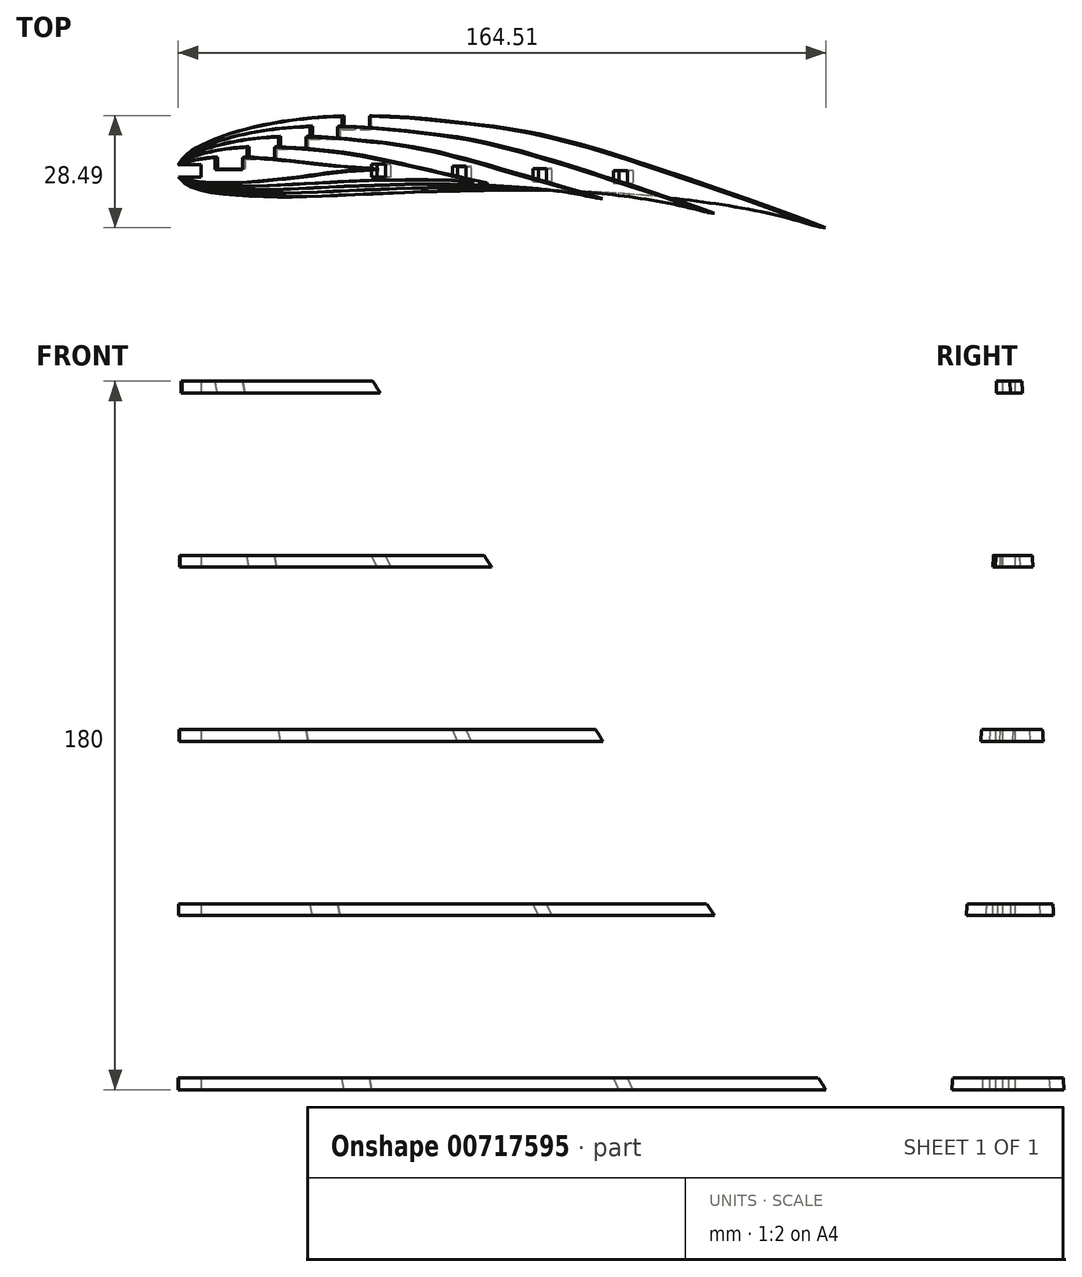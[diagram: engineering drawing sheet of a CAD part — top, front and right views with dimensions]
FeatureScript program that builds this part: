
annotation { "Feature Type Name" : "Feature", "Feature Type Description" : "" }
export const myFeature = defineFeature(function(context is Context, id is Id, definition is map)
    precondition{}
    {
        {
            var Q0;
            Q0=qCreatedBy(makeId("Top.planeOp"),FACE);
            var sketch = newSketch(context, id + "F0", { "sketchPlane" : qUnion([Q0])});
            skLineSegment(sketch, "E0", {"start": v(0.55, 2) * mm, "end": v(2.27, 4.06) * mm});
            skLineSegment(sketch, "E1", {"start": v(2.27, 4.06) * mm, "end": v(3.23, 4.97) * mm});
            skLineSegment(sketch, "E2", {"start": v(3.23, 4.97) * mm, "end": v(4.29, 5.76) * mm});
            skLineSegment(sketch, "E3", {"start": v(4.29, 5.76) * mm, "end": v(5.43, 6.47) * mm});
            skLineSegment(sketch, "E4", {"start": v(5.43, 6.47) * mm, "end": v(6.62, 7.1) * mm});
            skLineSegment(sketch, "E5", {"start": v(6.62, 7.1) * mm, "end": v(9.06, 8.22) * mm});
            skLineSegment(sketch, "E6", {"start": v(9.06, 8.22) * mm, "end": v(11.54, 9.18) * mm});
            skLineSegment(sketch, "E7", {"start": v(11.54, 9.18) * mm, "end": v(14.07, 10) * mm});
            skLineSegment(sketch, "E8", {"start": v(14.07, 10) * mm, "end": v(16.64, 10.72) * mm});
            skLineSegment(sketch, "E9", {"start": v(16.64, 10.72) * mm, "end": v(19.23, 11.35) * mm});
            skLineSegment(sketch, "E10", {"start": v(19.23, 11.35) * mm, "end": v(24.45, 12.45) * mm});
            skLineSegment(sketch, "E11", {"start": v(24.45, 12.45) * mm, "end": v(29.7, 13.34) * mm});
            skLineSegment(sketch, "E12", {"start": v(29.7, 13.34) * mm, "end": v(32.35, 13.68) * mm});
            skLineSegment(sketch, "E13", {"start": v(32.35, 13.68) * mm, "end": v(35, 13.95) * mm});
            skLineSegment(sketch, "E14", {"start": v(35, 13.95) * mm, "end": v(40.33, 14.29) * mm});
            skLineSegment(sketch, "E15", {"start": v(40.33, 14.29) * mm, "end": v(45.66, 14.43) * mm});
            skLineSegment(sketch, "E16", {"start": v(45.66, 14.43) * mm, "end": v(51, 14.4) * mm});
            skLineSegment(sketch, "E17", {"start": v(51, 14.4) * mm, "end": v(56.32, 14.18) * mm});
            skLineSegment(sketch, "E18", {"start": v(56.32, 14.18) * mm, "end": v(61.64, 13.83) * mm});
            skLineSegment(sketch, "E19", {"start": v(61.64, 13.83) * mm, "end": v(66.95, 13.36) * mm});
            skLineSegment(sketch, "E20", {"start": v(66.95, 13.36) * mm, "end": v(72.25, 12.79) * mm});
            skLineSegment(sketch, "E21", {"start": v(72.25, 12.79) * mm, "end": v(77.54, 12.1) * mm});
            skLineSegment(sketch, "E22", {"start": v(77.54, 12.1) * mm, "end": v(82.8, 11.26) * mm});
            skLineSegment(sketch, "E23", {"start": v(82.8, 11.26) * mm, "end": v(88.05, 10.28) * mm});
            skLineSegment(sketch, "E24", {"start": v(88.05, 10.28) * mm, "end": v(93.27, 9.2) * mm});
            skLineSegment(sketch, "E25", {"start": v(93.27, 9.2) * mm, "end": v(98.47, 8.03) * mm});
            skLineSegment(sketch, "E26", {"start": v(98.47, 8.03) * mm, "end": v(103.65, 6.76) * mm});
            skLineSegment(sketch, "E27", {"start": v(103.65, 6.76) * mm, "end": v(108.8, 5.4) * mm});
            skLineSegment(sketch, "E28", {"start": v(108.8, 5.4) * mm, "end": v(113.93, 3.92) * mm});
            skLineSegment(sketch, "E29", {"start": v(113.93, 3.92) * mm, "end": v(119.03, 2.37) * mm});
            skLineSegment(sketch, "E30", {"start": v(119.03, 2.37) * mm, "end": v(124.1, 0.73) * mm});
            skLineSegment(sketch, "E31", {"start": v(124.1, 0.73) * mm, "end": v(144.25, -6.3) * mm});
            skLineSegment(sketch, "E32", {"start": v(144.25, -6.3) * mm, "end": v(149.23, -8.12) * mm});
            skLineSegment(sketch, "E33", {"start": v(149.23, -8.12) * mm, "end": v(154.2, -10.04) * mm});
            skLineSegment(sketch, "E34", {"start": v(154.2, -10.04) * mm, "end": v(159.27, -11.88) * mm});
            skLineSegment(sketch, "E35", {"start": v(159.27, -11.88) * mm, "end": v(161.63, -12.76) * mm});
            skLineSegment(sketch, "E36", {"start": v(161.63, -12.76) * mm, "end": v(162.8, -13.22) * mm});
            skLineSegment(sketch, "E37", {"start": v(162.8, -13.22) * mm, "end": v(164.14, -13.73) * mm});
            skLineSegment(sketch, "E38", {"start": v(164.14, -13.73) * mm, "end": v(164.84, -13.98) * mm});
            skLineSegment(sketch, "E39", {"start": v(164.84, -13.98) * mm, "end": v(165, -14.04) * mm});
            skLineSegment(sketch, "E40", {"start": v(165, -14.04) * mm, "end": v(164.97, -14.04) * mm});
            skLineSegment(sketch, "E41", {"start": v(164.97, -14.04) * mm, "end": v(164.78, -14) * mm});
            skLineSegment(sketch, "E42", {"start": v(164.78, -14) * mm, "end": v(164.46, -13.9) * mm});
            skLineSegment(sketch, "E43", {"start": v(164.46, -13.9) * mm, "end": v(164.05, -13.77) * mm});
            skLineSegment(sketch, "E44", {"start": v(164.05, -13.77) * mm, "end": v(163.57, -13.62) * mm});
            skLineSegment(sketch, "E45", {"start": v(163.57, -13.62) * mm, "end": v(162.54, -13.3) * mm});
            skLineSegment(sketch, "E46", {"start": v(162.54, -13.3) * mm, "end": v(161.6, -13.02) * mm});
            skLineSegment(sketch, "E47", {"start": v(161.6, -13.02) * mm, "end": v(160.78, -12.78) * mm});
            skLineSegment(sketch, "E48", {"start": v(160.78, -12.78) * mm, "end": v(160.07, -12.58) * mm});
            skLineSegment(sketch, "E49", {"start": v(160.07, -12.58) * mm, "end": v(158.86, -12.25) * mm});
            skLineSegment(sketch, "E50", {"start": v(158.86, -12.25) * mm, "end": v(157.82, -11.99) * mm});
            skLineSegment(sketch, "E51", {"start": v(157.82, -11.99) * mm, "end": v(156.78, -11.74) * mm});
            skLineSegment(sketch, "E52", {"start": v(156.78, -11.74) * mm, "end": v(155.64, -11.47) * mm});
            skLineSegment(sketch, "E53", {"start": v(155.64, -11.47) * mm, "end": v(154.4, -11.18) * mm});
            skLineSegment(sketch, "E54", {"start": v(154.4, -11.18) * mm, "end": v(153.1, -10.88) * mm});
            skLineSegment(sketch, "E55", {"start": v(153.1, -10.88) * mm, "end": v(150.35, -10.26) * mm});
            skLineSegment(sketch, "E56", {"start": v(150.35, -10.26) * mm, "end": v(147.59, -9.68) * mm});
            skLineSegment(sketch, "E57", {"start": v(147.59, -9.68) * mm, "end": v(144.9, -9.16) * mm});
            skLineSegment(sketch, "E58", {"start": v(144.9, -9.16) * mm, "end": v(139.69, -8.28) * mm});
            skLineSegment(sketch, "E59", {"start": v(139.69, -8.28) * mm, "end": v(134.5, -7.54) * mm});
            skLineSegment(sketch, "E60", {"start": v(134.5, -7.54) * mm, "end": v(129.2, -6.88) * mm});
            skLineSegment(sketch, "E61", {"start": v(129.2, -6.88) * mm, "end": v(123.88, -6.3) * mm});
            skLineSegment(sketch, "E62", {"start": v(123.88, -6.3) * mm, "end": v(118.55, -5.81) * mm});
            skLineSegment(sketch, "E63", {"start": v(118.55, -5.81) * mm, "end": v(113.24, -5.41) * mm});
            skLineSegment(sketch, "E64", {"start": v(113.24, -5.41) * mm, "end": v(107.93, -5.1) * mm});
            skLineSegment(sketch, "E65", {"start": v(107.93, -5.1) * mm, "end": v(102.6, -4.84) * mm});
            skLineSegment(sketch, "E66", {"start": v(102.6, -4.84) * mm, "end": v(97.27, -4.67) * mm});
            skLineSegment(sketch, "E67", {"start": v(97.27, -4.67) * mm, "end": v(91.94, -4.58) * mm});
            skLineSegment(sketch, "E68", {"start": v(91.94, -4.58) * mm, "end": v(81.28, -4.6) * mm});
            skLineSegment(sketch, "E69", {"start": v(81.28, -4.6) * mm, "end": v(70.62, -4.85) * mm});
            skLineSegment(sketch, "E70", {"start": v(70.62, -4.85) * mm, "end": v(59.96, -5.2) * mm});
            skLineSegment(sketch, "E71", {"start": v(59.96, -5.2) * mm, "end": v(49.3, -5.55) * mm});
            skLineSegment(sketch, "E72", {"start": v(49.3, -5.55) * mm, "end": v(38.65, -5.97) * mm});
            skLineSegment(sketch, "E73", {"start": v(38.65, -5.97) * mm, "end": v(33.32, -6.17) * mm});
            skLineSegment(sketch, "E74", {"start": v(33.32, -6.17) * mm, "end": v(27.99, -6.29) * mm});
            skLineSegment(sketch, "E75", {"start": v(27.99, -6.29) * mm, "end": v(22.65, -6.26) * mm});
            skLineSegment(sketch, "E76", {"start": v(22.65, -6.26) * mm, "end": v(17.33, -6.03) * mm});
            skLineSegment(sketch, "E77", {"start": v(17.33, -6.03) * mm, "end": v(14.68, -5.81) * mm});
            skLineSegment(sketch, "E78", {"start": v(14.68, -5.81) * mm, "end": v(12.02, -5.5) * mm});
            skLineSegment(sketch, "E79", {"start": v(12.02, -5.5) * mm, "end": v(9.37, -5.1) * mm});
            skLineSegment(sketch, "E80", {"start": v(9.37, -5.1) * mm, "end": v(6.77, -4.56) * mm});
            skLineSegment(sketch, "E81", {"start": v(6.77, -4.56) * mm, "end": v(5.5, -4.23) * mm});
            skLineSegment(sketch, "E82", {"start": v(5.5, -4.23) * mm, "end": v(4.25, -3.83) * mm});
            skLineSegment(sketch, "E83", {"start": v(4.25, -3.83) * mm, "end": v(3.02, -3.3) * mm});
            skLineSegment(sketch, "E84", {"start": v(3.02, -3.3) * mm, "end": v(1.8, -2.61) * mm});
            skLineSegment(sketch, "E85", {"start": v(1.8, -2.61) * mm, "end": v(1.22, -2.19) * mm});
            skLineSegment(sketch, "E86", {"start": v(1.22, -2.19) * mm, "end": v(0.7, -1.71) * mm});
            skLineSegment(sketch, "E87", {"start": v(0.7, -1.71) * mm, "end": v(0.3, -1.19) * mm});
            skLineSegment(sketch, "E88", {"start": v(0.3, -1.19) * mm, "end": v(0.05, -0.62) * mm});
            skLineSegment(sketch, "E89", {"start": v(0.05, -0.62) * mm, "end": v(0, 0) * mm});
            skLineSegment(sketch, "E90", {"start": v(0, 0) * mm, "end": v(0.1, 0.65) * mm});
            skLineSegment(sketch, "E91", {"start": v(0.1, 0.65) * mm, "end": v(0.55, 2) * mm});
            skSolve(sketch);
        }
        {
            var Q0;
            Q0=qCreatedBy(makeId("Top.planeOp"),FACE);
            var sketch = newSketch(context, id + "F1", { "sketchPlane" : qUnion([Q0])});
            skPoint(sketch, "E92.0", {"position": v(0, 0) * mm});
            skPoint(sketch, "E92.1", {"position": v(3.23, 4.97) * mm});
            skPoint(sketch, "E92.2", {"position": v(0.55, 2) * mm});
            skPoint(sketch, "E92.3", {"position": v(16.64, 10.72) * mm});
            skPoint(sketch, "E92.4", {"position": v(45.66, 14.43) * mm});
            skPoint(sketch, "E92.5", {"position": v(77.54, 12.1) * mm});
            skPoint(sketch, "E92.6", {"position": v(108.8, 5.4) * mm});
            skPoint(sketch, "E92.7", {"position": v(165, -14.04) * mm});
            skPoint(sketch, "E92.8", {"position": v(156.78, -11.74) * mm});
            skPoint(sketch, "E92.9", {"position": v(129.2, -6.88) * mm});
            skPoint(sketch, "E92.10", {"position": v(91.94, -4.58) * mm});
            skPoint(sketch, "E92.11", {"position": v(49.3, -5.55) * mm});
            skPoint(sketch, "E92.12", {"position": v(27.99, -6.29) * mm});
            skPoint(sketch, "E92.13", {"position": v(12.02, -5.5) * mm});
            skPoint(sketch, "E92.14", {"position": v(3.02, -3.3) * mm});
            skFitSpline(sketch, "E93", {"points": [v(0.04, -0.4) * mm, v(0.59, 1.6) * mm, v(3.27, 4.57) * mm, v(16.67, 10.32) * mm, v(45.7, 14.03) * mm, v(77.58, 11.7) * mm, v(108.84, 4.99) * mm, v(165.04, -14.44) * mm, v(156.82, -12.14) * mm, v(129.25, -7.28) * mm, v(91.98, -4.98) * mm, v(49.34, -5.95) * mm, v(28.03, -6.69) * mm, v(12.06, -5.9) * mm, v(3.05, -3.7) * mm, v(0.04, -0.4) * mm]});
            skSolve(sketch);
        }
        {
            var Q0;
            Q0=qCreatedBy(makeId("Top.planeOp"),FACE);
            cPlane(context, id + "F2", {"entities" : qUnion([Q0]), "cplaneType" : CPlaneType.OFFSET, "offset" : 180 * mm, "width" : 150 * mm, "height" : 150 * mm});
        }
        {
            var Q0;
            Q0=qCreatedBy(id+"F2.planeOp",FACE);
            var sketch = newSketch(context, id + "F3", { "sketchPlane" : qUnion([Q0])});
            skLineSegment(sketch, "E94", {"start": v(0, 0) * mm, "end": v(0.15, 0.38) * mm});
            skLineSegment(sketch, "E95", {"start": v(0.15, 0.38) * mm, "end": v(0.35, 0.74) * mm});
            skLineSegment(sketch, "E96", {"start": v(0.35, 0.74) * mm, "end": v(0.46, 0.88) * mm});
            skLineSegment(sketch, "E97", {"start": v(0.46, 0.88) * mm, "end": v(0.6, 1.02) * mm});
            skLineSegment(sketch, "E98", {"start": v(0.6, 1.02) * mm, "end": v(0.92, 1.26) * mm});
            skLineSegment(sketch, "E99", {"start": v(0.92, 1.26) * mm, "end": v(1.29, 1.49) * mm});
            skLineSegment(sketch, "E100", {"start": v(1.29, 1.49) * mm, "end": v(1.63, 1.67) * mm});
            skLineSegment(sketch, "E101", {"start": v(1.63, 1.67) * mm, "end": v(2.36, 2) * mm});
            skLineSegment(sketch, "E102", {"start": v(2.36, 2) * mm, "end": v(2.87, 2.18) * mm});
            skLineSegment(sketch, "E103", {"start": v(2.87, 2.18) * mm, "end": v(3.88, 2.45) * mm});
            skLineSegment(sketch, "E104", {"start": v(3.88, 2.45) * mm, "end": v(5.05, 2.68) * mm});
            skLineSegment(sketch, "E105", {"start": v(5.05, 2.68) * mm, "end": v(7.03, 2.98) * mm});
            skLineSegment(sketch, "E106", {"start": v(7.03, 2.98) * mm, "end": v(7.78, 3.07) * mm});
            skLineSegment(sketch, "E107", {"start": v(7.78, 3.07) * mm, "end": v(8.62, 3.15) * mm});
            skLineSegment(sketch, "E108", {"start": v(8.62, 3.15) * mm, "end": v(10.95, 3.27) * mm});
            skLineSegment(sketch, "E109", {"start": v(10.95, 3.27) * mm, "end": v(11.82, 3.3) * mm});
            skLineSegment(sketch, "E110", {"start": v(11.82, 3.3) * mm, "end": v(13.41, 3.32) * mm});
            skLineSegment(sketch, "E111", {"start": v(13.41, 3.32) * mm, "end": v(14.62, 3.32) * mm});
            skLineSegment(sketch, "E112", {"start": v(14.62, 3.32) * mm, "end": v(16.6, 3.26) * mm});
            skLineSegment(sketch, "E113", {"start": v(16.6, 3.26) * mm, "end": v(18.58, 3.17) * mm});
            skLineSegment(sketch, "E114", {"start": v(18.58, 3.17) * mm, "end": v(21.4, 3.02) * mm});
            skLineSegment(sketch, "E115", {"start": v(21.4, 3.02) * mm, "end": v(22.8, 2.92) * mm});
            skLineSegment(sketch, "E116", {"start": v(22.8, 2.92) * mm, "end": v(24.58, 2.78) * mm});
            skLineSegment(sketch, "E117", {"start": v(24.58, 2.78) * mm, "end": v(27.06, 2.53) * mm});
            skLineSegment(sketch, "E118", {"start": v(27.06, 2.53) * mm, "end": v(31.42, 2.03) * mm});
            skLineSegment(sketch, "E119", {"start": v(31.42, 2.03) * mm, "end": v(35.63, 1.59) * mm});
            skLineSegment(sketch, "E120", {"start": v(35.63, 1.59) * mm, "end": v(37.3, 1.42) * mm});
            skLineSegment(sketch, "E121", {"start": v(37.3, 1.42) * mm, "end": v(39.54, 1.19) * mm});
            skLineSegment(sketch, "E122", {"start": v(39.54, 1.19) * mm, "end": v(42.05, 0.94) * mm});
            skLineSegment(sketch, "E123", {"start": v(42.05, 0.94) * mm, "end": v(43.06, 0.84) * mm});
            skLineSegment(sketch, "E124", {"start": v(43.06, 0.84) * mm, "end": v(44.5, 0.72) * mm});
            skLineSegment(sketch, "E125", {"start": v(44.5, 0.72) * mm, "end": v(45.29, 0.66) * mm});
            skLineSegment(sketch, "E126", {"start": v(45.29, 0.66) * mm, "end": v(45.98, 0.6) * mm});
            skLineSegment(sketch, "E127", {"start": v(45.98, 0.6) * mm, "end": v(46.75, 0.52) * mm});
            skLineSegment(sketch, "E128", {"start": v(46.75, 0.52) * mm, "end": v(47.13, 0.5) * mm});
            skLineSegment(sketch, "E129", {"start": v(47.13, 0.5) * mm, "end": v(47.54, 0.47) * mm});
            skLineSegment(sketch, "E130", {"start": v(47.54, 0.47) * mm, "end": v(48.16, 0.45) * mm});
            skLineSegment(sketch, "E131", {"start": v(48.16, 0.45) * mm, "end": v(48.52, 0.44) * mm});
            skLineSegment(sketch, "E132", {"start": v(48.52, 0.44) * mm, "end": v(49.07, 0.43) * mm});
            skLineSegment(sketch, "E133", {"start": v(49.07, 0.43) * mm, "end": v(49.32, 0.43) * mm});
            skLineSegment(sketch, "E134", {"start": v(49.32, 0.43) * mm, "end": v(49.55, 0.43) * mm});
            skLineSegment(sketch, "E135", {"start": v(49.55, 0.43) * mm, "end": v(49.74, 0.42) * mm});
            skLineSegment(sketch, "E136", {"start": v(49.74, 0.42) * mm, "end": v(49.88, 0.42) * mm});
            skLineSegment(sketch, "E137", {"start": v(49.88, 0.42) * mm, "end": v(49.97, 0.4) * mm});
            skLineSegment(sketch, "E138", {"start": v(49.97, 0.4) * mm, "end": v(50, 0.4) * mm});
            skLineSegment(sketch, "E139", {"start": v(50, 0.4) * mm, "end": v(49.95, 0.38) * mm});
            skLineSegment(sketch, "E140", {"start": v(49.95, 0.38) * mm, "end": v(49.84, 0.36) * mm});
            skLineSegment(sketch, "E141", {"start": v(49.84, 0.36) * mm, "end": v(49.68, 0.34) * mm});
            skLineSegment(sketch, "E142", {"start": v(49.68, 0.34) * mm, "end": v(49.48, 0.32) * mm});
            skLineSegment(sketch, "E143", {"start": v(49.48, 0.32) * mm, "end": v(49.25, 0.3) * mm});
            skLineSegment(sketch, "E144", {"start": v(49.25, 0.3) * mm, "end": v(48.99, 0.28) * mm});
            skLineSegment(sketch, "E145", {"start": v(48.99, 0.28) * mm, "end": v(48.44, 0.24) * mm});
            skLineSegment(sketch, "E146", {"start": v(48.44, 0.24) * mm, "end": v(48.16, 0.23) * mm});
            skLineSegment(sketch, "E147", {"start": v(48.16, 0.23) * mm, "end": v(47.48, 0.2) * mm});
            skLineSegment(sketch, "E148", {"start": v(47.48, 0.2) * mm, "end": v(47.07, 0.2) * mm});
            skLineSegment(sketch, "E149", {"start": v(47.07, 0.2) * mm, "end": v(46.7, 0.2) * mm});
            skLineSegment(sketch, "E150", {"start": v(46.7, 0.2) * mm, "end": v(45.98, 0.2) * mm});
            skLineSegment(sketch, "E151", {"start": v(45.98, 0.2) * mm, "end": v(45.22, 0.15) * mm});
            skLineSegment(sketch, "E152", {"start": v(45.22, 0.15) * mm, "end": v(44.43, 0.07) * mm});
            skLineSegment(sketch, "E153", {"start": v(44.43, 0.07) * mm, "end": v(43.06, -0.1) * mm});
            skLineSegment(sketch, "E154", {"start": v(43.06, -0.1) * mm, "end": v(42, -0.23) * mm});
            skLineSegment(sketch, "E155", {"start": v(42, -0.23) * mm, "end": v(39.6, -0.5) * mm});
            skLineSegment(sketch, "E156", {"start": v(39.6, -0.5) * mm, "end": v(35.63, -1) * mm});
            skLineSegment(sketch, "E157", {"start": v(35.63, -1) * mm, "end": v(31.42, -1.54) * mm});
            skLineSegment(sketch, "E158", {"start": v(31.42, -1.54) * mm, "end": v(27.1, -2.08) * mm});
            skLineSegment(sketch, "E159", {"start": v(27.1, -2.08) * mm, "end": v(24.56, -2.35) * mm});
            skLineSegment(sketch, "E160", {"start": v(24.56, -2.35) * mm, "end": v(22.84, -2.53) * mm});
            skLineSegment(sketch, "E161", {"start": v(22.84, -2.53) * mm, "end": v(19.79, -2.83) * mm});
            skLineSegment(sketch, "E162", {"start": v(19.79, -2.83) * mm, "end": v(18.63, -2.92) * mm});
            skLineSegment(sketch, "E163", {"start": v(18.63, -2.92) * mm, "end": v(16.6, -3.05) * mm});
            skLineSegment(sketch, "E164", {"start": v(16.6, -3.05) * mm, "end": v(14.67, -3.12) * mm});
            skLineSegment(sketch, "E165", {"start": v(14.67, -3.12) * mm, "end": v(13.4, -3.16) * mm});
            skLineSegment(sketch, "E166", {"start": v(13.4, -3.16) * mm, "end": v(11.8, -3.18) * mm});
            skLineSegment(sketch, "E167", {"start": v(11.8, -3.18) * mm, "end": v(11, -3.17) * mm});
            skLineSegment(sketch, "E168", {"start": v(11, -3.17) * mm, "end": v(7.83, -3.02) * mm});
            skLineSegment(sketch, "E169", {"start": v(7.83, -3.02) * mm, "end": v(7.02, -2.94) * mm});
            skLineSegment(sketch, "E170", {"start": v(7.02, -2.94) * mm, "end": v(5.1, -2.68) * mm});
            skLineSegment(sketch, "E171", {"start": v(5.1, -2.68) * mm, "end": v(4.65, -2.6) * mm});
            skLineSegment(sketch, "E172", {"start": v(4.65, -2.6) * mm, "end": v(3.87, -2.43) * mm});
            skLineSegment(sketch, "E173", {"start": v(3.87, -2.43) * mm, "end": v(2.92, -2.18) * mm});
            skLineSegment(sketch, "E174", {"start": v(2.92, -2.18) * mm, "end": v(2.34, -1.98) * mm});
            skLineSegment(sketch, "E175", {"start": v(2.34, -1.98) * mm, "end": v(1.6, -1.67) * mm});
            skLineSegment(sketch, "E176", {"start": v(1.6, -1.67) * mm, "end": v(1.34, -1.54) * mm});
            skLineSegment(sketch, "E177", {"start": v(1.34, -1.54) * mm, "end": v(0.88, -1.28) * mm});
            skLineSegment(sketch, "E178", {"start": v(0.88, -1.28) * mm, "end": v(0.56, -1.04) * mm});
            skLineSegment(sketch, "E179", {"start": v(0.56, -1.04) * mm, "end": v(0.43, -0.9) * mm});
            skLineSegment(sketch, "E180", {"start": v(0.43, -0.9) * mm, "end": v(0.35, -0.8) * mm});
            skLineSegment(sketch, "E181", {"start": v(0.35, -0.8) * mm, "end": v(0.13, -0.38) * mm});
            skLineSegment(sketch, "E182", {"start": v(0.13, -0.38) * mm, "end": v(0, 0) * mm});
            skSolve(sketch);
        }
        {
            var Q0;
            Q0=qCreatedBy(id+"F2.planeOp",FACE);
            var sketch = newSketch(context, id + "F4", { "sketchPlane" : qUnion([Q0])});
            skPoint(sketch, "E183.0", {"position": v(0, 0) * mm});
            skPoint(sketch, "E183.1", {"position": v(0.92, 1.26) * mm});
            skPoint(sketch, "E183.2", {"position": v(2.36, 2) * mm});
            skPoint(sketch, "E183.3", {"position": v(7.03, 2.98) * mm});
            skPoint(sketch, "E183.4", {"position": v(14.62, 3.32) * mm});
            skPoint(sketch, "E183.5", {"position": v(27.06, 2.53) * mm});
            skPoint(sketch, "E183.6", {"position": v(39.54, 1.19) * mm});
            skPoint(sketch, "E183.7", {"position": v(49.97, 0.4) * mm});
            skPoint(sketch, "E183.8", {"position": v(44.43, 0.07) * mm});
            skPoint(sketch, "E183.9", {"position": v(35.63, -1) * mm});
            skPoint(sketch, "E183.10", {"position": v(27.1, -2.08) * mm});
            skPoint(sketch, "E183.11", {"position": v(16.6, -3.05) * mm});
            skPoint(sketch, "E183.12", {"position": v(7.83, -3.02) * mm});
            skPoint(sketch, "E183.13", {"position": v(3.87, -2.43) * mm});
            skPoint(sketch, "E183.14", {"position": v(0.88, -1.28) * mm});
            skFitSpline(sketch, "E184", {"points": [v(0, 0.07) * mm, v(0.92, 1.34) * mm, v(2.36, 2.06) * mm, v(7.04, 3.05) * mm, v(14.62, 3.4) * mm, v(27.06, 2.6) * mm, v(39.55, 1.26) * mm, v(49.98, 0.48) * mm, v(44.43, 0.14) * mm, v(35.63, -0.92) * mm, v(27.1, -2.01) * mm, v(16.6, -2.97) * mm, v(7.83, -2.95) * mm, v(3.87, -2.36) * mm, v(0.89, -1.2) * mm, v(0, 0.07) * mm]});
            skSolve(sketch);
        }
        {
            var Q0;
            Q0=makeQuery(id+"F4.imprint","IMPRINT",FACE,{"disambiguationData":[TD([[makeQuery(id+"F4.imprint","IMPRINT",EDGE,{"derivedFrom":sQuery(id+"F4.wireOp",EDGE,"E184")}),-1.0]])]});
            var Q1;
            Q1=makeQuery(id+"F1.imprint","IMPRINT",FACE,{"disambiguationData":[TD([[makeQuery(id+"F1.imprint","IMPRINT",EDGE,{"derivedFrom":sQuery(id+"F1.wireOp",EDGE,"E93")}),-1.0]])]});
            loft(context, id + "F5", {"sheetProfilesArray" : [{ "sheetProfileEntities" : qUnion([Q0]) }, { "sheetProfileEntities" : qUnion([Q1]) }]});
        }
        {
            var Q0;
            Q0=qCreatedBy(makeId("Front.planeOp"),FACE);
            var sketch = newSketch(context, id + "F6", { "sketchPlane" : qUnion([Q0])});
            skLineSegment(sketch, "E185", {"start": v(0, 0) * mm, "end": v(0, 3) * mm, "construction": true});
            skLineSegment(sketch, "E186", {"start": v(0, 3) * mm, "end": v(-5, 3) * mm});
            skLineSegment(sketch, "E187.bottom", {"start": v(-5, 3) * mm, "end": v(175, 3) * mm});
            skLineSegment(sketch, "E187.top", {"start": v(-5, 44.25) * mm, "end": v(175, 44.25) * mm});
            skLineSegment(sketch, "E187.left", {"start": v(-5, 3) * mm, "end": v(-5, 44.25) * mm});
            skLineSegment(sketch, "E187.right", {"start": v(175, 3) * mm, "end": v(175, 44.25) * mm});
            skLineSegment(sketch, "E188", {"start": v(-5, 44.25) * mm, "end": v(-5, 47.25) * mm, "construction": true});
            skLineSegment(sketch, "E189.bottom", {"start": v(-5, 47.25) * mm, "end": v(175, 47.25) * mm});
            skLineSegment(sketch, "E189.top", {"start": v(-5, 88.5) * mm, "end": v(175, 88.5) * mm});
            skLineSegment(sketch, "E189.left", {"start": v(-5, 47.25) * mm, "end": v(-5, 88.5) * mm});
            skLineSegment(sketch, "E189.right", {"start": v(175, 47.25) * mm, "end": v(175, 88.5) * mm});
            skLineSegment(sketch, "E190", {"start": v(-5, 88.5) * mm, "end": v(-5, 91.5) * mm, "construction": true});
            skLineSegment(sketch, "E191.bottom", {"start": v(-5, 91.5) * mm, "end": v(175, 91.5) * mm});
            skLineSegment(sketch, "E191.top", {"start": v(-5, 132.75) * mm, "end": v(175, 132.75) * mm});
            skLineSegment(sketch, "E191.left", {"start": v(-5, 91.5) * mm, "end": v(-5, 132.75) * mm});
            skLineSegment(sketch, "E191.right", {"start": v(175, 91.5) * mm, "end": v(175, 132.75) * mm});
            skLineSegment(sketch, "E192", {"start": v(-5, 132.75) * mm, "end": v(-5, 135.75) * mm, "construction": true});
            skLineSegment(sketch, "E193.bottom", {"start": v(-5, 135.75) * mm, "end": v(175, 135.75) * mm});
            skLineSegment(sketch, "E193.top", {"start": v(-5, 177) * mm, "end": v(175, 177) * mm});
            skLineSegment(sketch, "E193.left", {"start": v(-5, 135.75) * mm, "end": v(-5, 177) * mm});
            skLineSegment(sketch, "E193.right", {"start": v(175, 135.75) * mm, "end": v(175, 177) * mm});
            skLineSegment(sketch, "E194", {"start": v(0, 3) * mm, "end": v(0, 0) * mm, "construction": true});
            skSolve(sketch);
        }
        {
            var Q0;
            Q0 = qSketchRegion(id + "F6", true);
            extrude(context, id + "F7", {"entities" : qUnion([Q0]), "operationType" : NewBodyOperationType.REMOVE, "oppositeDirection" : true, "depth" : 50 * mm, "offsetDistance" : 25 * mm, "hasSecondDirection" : true, "secondDirectionOppositeDirection" : false, "secondDirectionDepth" : 50 * mm});
        }
        {
            var Q0;
            Q0=qCreatedBy(makeId("Top.planeOp"),FACE);
            var sketch = newSketch(context, id + "F8", { "sketchPlane" : qUnion([Q0])});
            skLineSegment(sketch, "E195", {"start": v(-1.3, 1.59) * mm, "end": v(6.35, 1.59) * mm});
            skLineSegment(sketch, "E196", {"start": v(-1.3, -1.59) * mm, "end": v(6.35, -1.59) * mm});
            skLineSegment(sketch, "E197", {"start": v(-1.3, -1.59) * mm, "end": v(-1.3, 1.59) * mm});
            skLineSegment(sketch, "E198", {"start": v(6.35, -1.59) * mm, "end": v(6.35, 1.59) * mm});
            skLineSegment(sketch, "E199", {"start": v(0, 0) * mm, "end": v(6.35, 0) * mm, "construction": true});
            skLineSegment(sketch, "E200", {"start": v(-1.3, 0) * mm, "end": v(6.35, 0) * mm, "construction": true});
            skSolve(sketch);
        }
        {
            var Q0;
            Q0=makeQuery(id+"F8.imprint","IMPRINT",FACE,{"disambiguationData":[TD([[makeQuery(id+"F8.imprint","IMPRINT",EDGE,{"derivedFrom":sQuery(id+"F8.wireOp",EDGE,"E195")}),-1.0]])]});
            extrude(context, id + "F9", {"entities" : qUnion([Q0]), "operationType" : NewBodyOperationType.REMOVE, "depth" : 250 * mm, "offsetDistance" : 25 * mm});
        }
        {
            var Q0;
            Q0=qCreatedBy(makeId("Top.planeOp"),FACE);
            var sketch = newSketch(context, id + "F10", { "sketchPlane" : qUnion([Q0])});
            skFitSpline(sketch, "E201.0", {"points": [v(0, 0.07) * mm, v(0.01, 0.29) * mm, v(0.06, 0.53) * mm, v(0.16, 0.78) * mm, v(0.16, 0.79) * mm, v(0.24, 0.98) * mm, v(0.35, 1.2) * mm, v(0.51, 1.47) * mm, v(0.52, 1.49) * mm, v(0.83, 2.01) * mm, v(1.17, 2.5) * mm, v(1.54, 2.94) * mm, v(1.56, 2.97) * mm, v(2.01, 3.5) * mm, v(2.57, 4.03) * mm, v(3.21, 4.52) * mm, v(3.24, 4.55) * mm, v(3.91, 5.06) * mm, v(4.78, 5.6) * mm, v(5.8, 6.16) * mm, v(5.85, 6.19) * mm, v(6.82, 6.7) * mm, v(7.97, 7.25) * mm, v(9.25, 7.78) * mm, v(9.31, 7.81) * mm, v(10.54, 8.32) * mm, v(11.92, 8.83) * mm, v(13.39, 9.32) * mm, v(13.46, 9.35) * mm, v(16.3, 10.28) * mm, v(19.54, 11.13) * mm, v(23.03, 11.83) * mm, v(23.21, 11.86) * mm, v(26.54, 12.52) * mm, v(30.23, 13.06) * mm, v(34.09, 13.43) * mm, v(34.3, 13.45) * mm, v(37.99, 13.8) * mm, v(41.96, 14) * mm, v(46, 14.03) * mm, v(46.2, 14.03) * mm, v(49.77, 14.04) * mm, v(53.82, 13.91) * mm, v(58.18, 13.63) * mm, v(58.41, 13.62) * mm, v(61.82, 13.4) * mm, v(65.72, 13.05) * mm, v(69.95, 12.59) * mm, v(70.17, 12.56) * mm, v(71.77, 12.39) * mm, v(73.58, 12.18) * mm, v(75.53, 11.95) * mm, v(75.64, 11.93) * mm, v(77.52, 11.7) * mm, v(79.23, 11.49) * mm, v(80.65, 11.3) * mm, v(80.72, 11.3) * mm, v(82.42, 11.07) * mm, v(84.05, 10.84) * mm, v(85.51, 10.6) * mm, v(85.6, 10.6) * mm, v(87.21, 10.34) * mm, v(88.89, 10.04) * mm, v(90.53, 9.72) * mm, v(90.61, 9.7) * mm, v(92.32, 9.36) * mm, v(94.16, 8.96) * mm, v(96.06, 8.5) * mm, v(96.16, 8.48) * mm, v(98.07, 8.02) * mm, v(100.2, 7.47) * mm, v(102.46, 6.85) * mm, v(102.58, 6.81) * mm, v(104.81, 6.2) * mm, v(107.36, 5.45) * mm, v(110.1, 4.6) * mm, v(110.25, 4.56) * mm, v(112.8, 3.77) * mm, v(115.79, 2.82) * mm, v(119.09, 1.75) * mm, v(119.26, 1.7) * mm, v(124.8, -0.12) * mm, v(131.28, -2.3) * mm, v(138.45, -4.8) * mm, v(138.82, -4.93) * mm, v(141.71, -5.93) * mm, v(144.77, -7) * mm, v(147.82, -8.1) * mm, v(147.99, -8.15) * mm, v(150.61, -9.09) * mm, v(153.24, -10.03) * mm, v(155.7, -10.92) * mm, v(155.82, -10.97) * mm, v(158, -11.76) * mm, v(159.95, -12.48) * mm, v(161.56, -13.08) * mm, v(161.64, -13.11) * mm, v(163.12, -13.66) * mm, v(164.18, -14.07) * mm, v(164.73, -14.3) * mm, v(164.75, -14.31) * mm, v(165, -14.42) * mm, v(165.1, -14.47) * mm, v(165.08, -14.48) * mm, v(165.08, -14.48) * mm, v(165.05, -14.49) * mm, v(164.9, -14.45) * mm, v(164.6, -14.37) * mm, v(164.58, -14.37) * mm, v(164.37, -14.3) * mm, v(163.99, -14.2) * mm, v(163.43, -14.03) * mm, v(163.4, -14.02) * mm, v(162.51, -13.76) * mm, v(161.92, -13.58) * mm, v(161.7, -13.52) * mm, v(161.7, -13.51) * mm, v(160.1, -13.05) * mm, v(158.62, -12.62) * mm, v(157.32, -12.28) * mm, v(157.25, -12.26) * mm, v(155.75, -11.86) * mm, v(154.1, -11.45) * mm, v(152.4, -11.06) * mm, v(152.3, -11.04) * mm, v(149.2, -10.34) * mm, v(145.68, -9.65) * mm, v(141.9, -9.03) * mm, v(141.72, -9) * mm, v(138.38, -8.45) * mm, v(134.62, -7.92) * mm, v(130.6, -7.44) * mm, v(130.4, -7.41) * mm, v(126.66, -6.96) * mm, v(122.7, -6.56) * mm, v(118.7, -6.22) * mm, v(118.5, -6.2) * mm, v(114.6, -5.88) * mm, v(110.41, -5.6) * mm, v(106.18, -5.4) * mm, v(105.96, -5.39) * mm, v(101.83, -5.19) * mm, v(97.39, -5.05) * mm, v(92.86, -4.99) * mm, v(92.62, -4.99) * mm, v(85, -4.89) * mm, v(75.68, -5) * mm, v(65.03, -5.33) * mm, v(64.48, -5.35) * mm, v(60.67, -5.47) * mm, v(56.4, -5.64) * mm, v(51.9, -5.83) * mm, v(51.64, -5.84) * mm, v(50.19, -5.9) * mm, v(48.33, -6) * mm, v(46.13, -6.1) * mm, v(46, -6.1) * mm, v(43.6, -6.21) * mm, v(41.85, -6.3) * mm, v(40.95, -6.33) * mm, v(40.9, -6.34) * mm, v(39.2, -6.41) * mm, v(37.61, -6.48) * mm, v(36.26, -6.53) * mm, v(36.2, -6.53) * mm, v(34.67, -6.58) * mm, v(33.18, -6.62) * mm, v(31.8, -6.65) * mm, v(31.74, -6.65) * mm, v(30.3, -6.68) * mm, v(28.85, -6.7) * mm, v(27.46, -6.69) * mm, v(27.38, -6.69) * mm, v(26.02, -6.68) * mm, v(24.58, -6.66) * mm, v(23.13, -6.61) * mm, v(23.05, -6.61) * mm, v(20.32, -6.53) * mm, v(17.55, -6.38) * mm, v(14.9, -6.17) * mm, v(14.77, -6.16) * mm, v(13.47, -6.05) * mm, v(12.21, -5.93) * mm, v(11.07, -5.8) * mm, v(11, -5.8) * mm, v(10.4, -5.72) * mm, v(9.82, -5.65) * mm, v(9.3, -5.57) * mm, v(9.26, -5.57) * mm, v(8.7, -5.48) * mm, v(8.16, -5.39) * mm, v(7.65, -5.29) * mm, v(7.62, -5.28) * mm, v(6.56, -5.07) * mm, v(5.58, -4.8) * mm, v(4.73, -4.49) * mm, v(4.69, -4.47) * mm, v(4.25, -4.31) * mm, v(3.83, -4.12) * mm, v(3.43, -3.92) * mm, v(3.4, -3.9) * mm, v(3.03, -3.7) * mm, v(2.65, -3.47) * mm, v(2.29, -3.22) * mm, v(2.27, -3.2) * mm, v(1.94, -2.96) * mm, v(1.62, -2.7) * mm, v(1.32, -2.41) * mm, v(1.3, -2.4) * mm, v(1.04, -2.13) * mm, v(0.8, -1.85) * mm, v(0.59, -1.56) * mm, v(0.58, -1.55) * mm, v(0.38, -1.27) * mm, v(0.23, -1) * mm, v(0.13, -0.72) * mm, v(0.13, -0.7) * mm, v(0.03, -0.44) * mm, v(-0.01, -0.18) * mm, v(0, 0.07) * mm]});
            skLineSegment(sketch, "E202.bottom", {"start": v(42.68, 10.55) * mm, "end": v(49.68, 10.55) * mm});
            skLineSegment(sketch, "E202.top", {"start": v(42.68, 16.22) * mm, "end": v(49.68, 16.22) * mm});
            skLineSegment(sketch, "E202.left", {"start": v(42.68, 10.55) * mm, "end": v(42.68, 16.22) * mm});
            skLineSegment(sketch, "E202.right", {"start": v(49.68, 10.55) * mm, "end": v(49.68, 16.22) * mm});
            skSolve(sketch);
        }
        {
            var Q0;
            Q0=makeQuery(id+"F5.opLoft","CAP_FACE",FACE,{"disambiguationData":[OSD([makeQuery(id+"F4.imprint","IMPRINT",FACE,{"disambiguationData":[TD([[makeQuery(id+"F4.imprint","IMPRINT",EDGE,{"derivedFrom":sQuery(id+"F4.wireOp",EDGE,"E184")}),-1.0]])]})])],"isStart":true});
            var sketch = newSketch(context, id + "F11", { "sketchPlane" : qUnion([Q0])});
            skFitSpline(sketch, "E203.0", {"points": [v(1.5, -1.59) * mm, v(1.75, -1.7) * mm, v(2.24, -1.91) * mm, v(3, -2.16) * mm, v(3.76, -2.37) * mm, v(4.79, -2.6) * mm, v(6.1, -2.83) * mm, v(7.67, -3) * mm, v(9.26, -3.08) * mm, v(11.37, -3.15) * mm, v(14, -3.15) * mm, v(17.18, -3.04) * mm, v(20.35, -2.83) * mm, v(23.5, -2.55) * mm, v(26.66, -2.22) * mm, v(29.8, -1.87) * mm, v(32.96, -1.52) * mm, v(35.58, -1.2) * mm, v(37.68, -0.93) * mm, v(39.25, -0.72) * mm, v(40.82, -0.53) * mm, v(42.4, -0.34) * mm, v(43.71, -0.22) * mm, v(44.76, -0.13) * mm, v(45.56, -0.07) * mm, v(46.35, -0.03) * mm, v(47.14, 0.01) * mm, v(47.93, 0.04) * mm, v(48.6, 0.07) * mm, v(49.12, 0.09) * mm, v(49.52, 0.1) * mm, v(49.91, 0.1) * mm, v(50.24, 0.12) * mm, v(50.5, 0.13) * mm, v(50.7, 0.13) * mm, v(50.9, 0.14) * mm, v(51.1, 0.15) * mm, v(51.27, 0.16) * mm, v(51.4, 0.16) * mm, v(51.5, 0.17) * mm, v(51.58, 0.17) * mm, v(51.65, 0.18) * mm, v(51.7, 0.18) * mm, v(51.75, 0.19) * mm, v(51.79, 0.2) * mm, v(51.82, 0.2) * mm, v(51.85, 0.2) * mm, v(51.87, 0.2) * mm, v(51.88, 0.21) * mm, v(51.9, 0.22) * mm, v(51.9, 0.23) * mm, v(51.9, 0.23) * mm, v(51.88, 0.24) * mm, v(51.86, 0.25) * mm, v(51.83, 0.25) * mm, v(51.8, 0.26) * mm, v(51.76, 0.27) * mm, v(51.7, 0.28) * mm, v(51.61, 0.3) * mm, v(51.51, 0.3) * mm, v(51.41, 0.32) * mm, v(51.28, 0.33) * mm, v(51.12, 0.35) * mm, v(50.92, 0.37) * mm, v(50.72, 0.4) * mm, v(50.52, 0.4) * mm, v(50.26, 0.43) * mm, v(49.92, 0.46) * mm, v(49.53, 0.5) * mm, v(49.13, 0.53) * mm, v(48.6, 0.57) * mm, v(47.94, 0.63) * mm, v(47.14, 0.7) * mm, v(46.34, 0.75) * mm, v(45.55, 0.82) * mm, v(44.75, 0.88) * mm, v(43.7, 0.97) * mm, v(42.37, 1.09) * mm, v(40.78, 1.24) * mm, v(39.19, 1.4) * mm, v(37.6, 1.58) * mm, v(35.49, 1.83) * mm, v(32.85, 2.17) * mm, v(29.68, 2.56) * mm, v(26.5, 2.9) * mm, v(23.32, 3.16) * mm, v(20.13, 3.38) * mm, v(16.94, 3.53) * mm, v(13.75, 3.6) * mm, v(11.09, 3.56) * mm, v(8.97, 3.4) * mm, v(7.38, 3.22) * mm, v(5.8, 2.97) * mm, v(4.23, 2.65) * mm, v(2.94, 2.32) * mm, v(2.06, 2.02) * mm, v(1.58, 1.8) * mm, v(1.35, 1.66) * mm, v(1.24, 1.59) * mm]});
            skLineSegment(sketch, "E204", {"start": v(13.25, 3.58) * mm, "end": v(13.25, 0.28) * mm, "construction": true});
            skLineSegment(sketch, "E205", {"start": v(13.25, 0.28) * mm, "end": v(16.55, 0.28) * mm, "construction": true});
            skLineSegment(sketch, "E206", {"start": v(13.25, 0.28) * mm, "end": v(9.95, 0.28) * mm, "construction": true});
            skLineSegment(sketch, "E207.bottom", {"start": v(16.55, 0.28) * mm, "end": v(9.95, 0.28) * mm});
            skLineSegment(sketch, "E207.top", {"start": v(16.55, 5.01) * mm, "end": v(9.95, 5.01) * mm});
            skLineSegment(sketch, "E207.left", {"start": v(16.55, 0.28) * mm, "end": v(16.55, 5.01) * mm});
            skLineSegment(sketch, "E207.right", {"start": v(9.95, 0.28) * mm, "end": v(9.95, 5.01) * mm});
            skSolve(sketch);
        }
        {
            var Q0;
            Q0=sQuery(id+"F10.wireOp",VERTEX,"E202.left.start");
            var Q1;
            Q1=sQuery(id+"F10.wireOp",VERTEX,"E202.left.end");
            var Q2;
            Q2=sQuery(id+"F11.wireOp",VERTEX,"E207.bottom.end");
            cPlane(context, id + "F12", {"entities" : qUnion([Q0, Q1, Q2]), "cplaneType" : CPlaneType.THREE_POINT, "offset" : 25 * mm, "width" : 150 * mm, "height" : 150 * mm});
        }
        {
            var Q0;
            Q0=qCreatedBy(id+"F12.planeOp",FACE);
            var sketch = newSketch(context, id + "F13", { "sketchPlane" : qUnion([Q0])});
            skPoint(sketch, "E208.0", {"position": v(-10.55, -7.64) * mm});
            skPoint(sketch, "E208.1", {"position": v(-0.28, 175.32) * mm});
            skLineSegment(sketch, "E209", {"start": v(-10.55, -7.64) * mm, "end": v(-0.28, 175.32) * mm});
            skSolve(sketch);
        }
        {
            var Q0;
            Q0 = qSketchRegion(id + "F10", true);
            var Q1;
            Q1=sQuery(id+"F13.wireOp",EDGE,"E209");
            sweep(context, id + "F14", {"operationType" : NewBodyOperationType.REMOVE, "profiles" : qUnion([Q0]), "path" : qUnion([Q1])});
        }
        {
            var Q0;
            Q0=makeQuery(id+"F5.opLoft","CAP_FACE",FACE,{"disambiguationData":[OSD([makeQuery(id+"F1.imprint","IMPRINT",FACE,{"disambiguationData":[TD([[makeQuery(id+"F1.imprint","IMPRINT",EDGE,{"derivedFrom":sQuery(id+"F1.wireOp",EDGE,"E93")}),-1.0]])]})])],"isStart":true});
            var sketch = newSketch(context, id + "F15", { "sketchPlane" : qUnion([Q0])});
            skLineSegment(sketch, "E210.bottom", {"start": v(116.05, 0) * mm, "end": v(112.55, 0) * mm});
            skLineSegment(sketch, "E210.top", {"start": v(116.05, 3.3) * mm, "end": v(112.55, 3.3) * mm});
            skLineSegment(sketch, "E210.left", {"start": v(116.05, 0) * mm, "end": v(116.05, 3.3) * mm});
            skLineSegment(sketch, "E210.right", {"start": v(112.55, 0) * mm, "end": v(112.55, 3.3) * mm});
            skSolve(sketch);
        }
        {
            var Q0;
            Q0=makeQuery(id+"F7.boolean.opBoolean","COPY",FACE,{"derivedFrom":makeQuery(id+"F7.opExtrude","SWEPT_FACE",FACE,{"disambiguationData":[OSD([sQuery(id+"F6.wireOp",EDGE,"E193.bottom")])]})});
            var sketch = newSketch(context, id + "F16", { "sketchPlane" : qUnion([Q0])});
            skLineSegment(sketch, "E211.bottom", {"start": v(49.7, 1.67) * mm, "end": v(53.2, 1.67) * mm});
            skLineSegment(sketch, "E211.top", {"start": v(49.7, -1.63) * mm, "end": v(53.2, -1.63) * mm});
            skLineSegment(sketch, "E211.left", {"start": v(49.7, 1.67) * mm, "end": v(49.7, -1.63) * mm});
            skLineSegment(sketch, "E211.right", {"start": v(53.2, 1.67) * mm, "end": v(53.2, -1.63) * mm});
            skSolve(sketch);
        }
        {
            var Q0;
            Q0 = qSketchRegion(id + "F15", true);
            var Q1;
            Q1 = qSketchRegion(id + "F16", true);
            loft(context, id + "F17", {"operationType" : NewBodyOperationType.REMOVE, "sheetProfilesArray" : [{ "sheetProfileEntities" : qUnion([Q0]) }, { "sheetProfileEntities" : qUnion([Q1]) }]});
        }
    });
